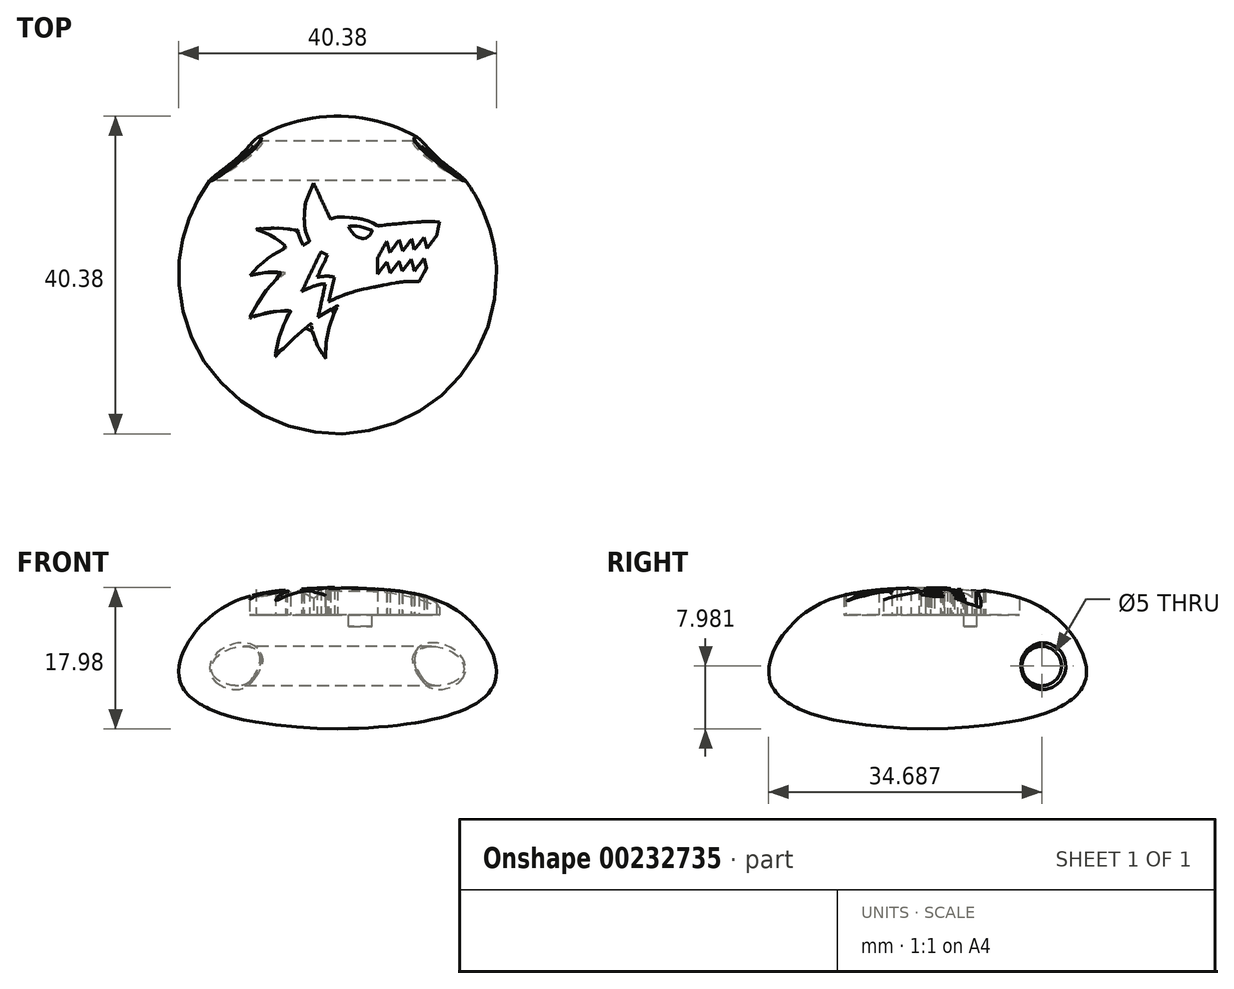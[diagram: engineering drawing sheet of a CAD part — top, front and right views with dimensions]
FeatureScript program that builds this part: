
annotation { "Feature Type Name" : "Feature", "Feature Type Description" : "" }
export const myFeature = defineFeature(function(context is Context, id is Id, definition is map)
    precondition{}
    {
        {
            var Q0;
            Q0=qCreatedBy(makeId("Front.planeOp"),FACE);
            var sketch = newSketch(context, id + "F0", { "sketchPlane" : qUnion([Q0])});
            skFitSpline(sketch, "E0", {"points": [v(0, 12) * mm, v(15.05, 9.11) * mm, v(20, 0) * mm, v(0, -6) * mm], "startDerivative": vector(53.57, -2.67) * mm, "endDerivative": vector(-80.04, -1.37) * mm});
            skLineSegment(sketch, "E1", {"start": v(0, 0) * mm, "end": v(0, -6) * mm});
            skLineSegment(sketch, "E2", {"start": v(0, 0) * mm, "end": v(0, 12) * mm});
            skLineSegment(sketch, "E3", {"start": v(0, 0) * mm, "end": v(20, 0) * mm});
            skSolve(sketch);
        }
        {
            var Q0;
            Q0 = qSketchRegion(id + "F0", true);
            var Q1;
            Q1=sQuery(id+"F0.wireOp",EDGE,"E2");
            revolve(context, id + "F1", {"entities" : qUnion([Q0]), "axis" : qUnion([Q1]), "revolveType" : RevolveType.FULL});
        }
        {
            var Q0;
            Q0=qCreatedBy(makeId("Top.planeOp"),FACE);
            var sketch = newSketch(context, id + "F2", { "sketchPlane" : qUnion([Q0])});
            skLineSegment(sketch, "E4", {"start": v(-3.05, 11.68) * mm, "end": v(-0.92, 7.1) * mm});
            skFitSpline(sketch, "E5", {"points": [v(-0.92, 7.1) * mm, v(0, 7.34) * mm, v(1.82, 7.27) * mm, v(3.9, 6.84) * mm, v(5.2, 6.21) * mm, v(5.35, 6.24) * mm, v(7.78, 6.52) * mm, v(10.2, 6.73) * mm, v(12.15, 6.78) * mm, v(12.94, 6.73) * mm], "startDerivative": vector(9.2, 3.23) * mm, "endDerivative": vector(8.4, -0.74) * mm});
            skLineSegment(sketch, "E6", {"start": v(12.94, 6.73) * mm, "end": v(12.59, 5) * mm});
            skLineSegment(sketch, "E7", {"start": v(12.59, 5) * mm, "end": v(11.37, 3.38) * mm});
            skLineSegment(sketch, "E8", {"start": v(11.37, 3.38) * mm, "end": v(10.98, 4.75) * mm});
            skLineSegment(sketch, "E9", {"start": v(10.98, 4.75) * mm, "end": v(9.74, 3.2) * mm});
            skLineSegment(sketch, "E10", {"start": v(9.74, 3.2) * mm, "end": v(9.42, 4.54) * mm});
            skLineSegment(sketch, "E11", {"start": v(9.42, 4.54) * mm, "end": v(8.26, 3.04) * mm});
            skLineSegment(sketch, "E12", {"start": v(8.26, 3.04) * mm, "end": v(7.83, 4.46) * mm});
            skLineSegment(sketch, "E13", {"start": v(7.83, 4.46) * mm, "end": v(6.64, 2.83) * mm});
            skLineSegment(sketch, "E14", {"start": v(6.64, 2.83) * mm, "end": v(6.23, 4.27) * mm});
            skLineSegment(sketch, "E15", {"start": v(6.23, 4.27) * mm, "end": v(5.1, 2.17) * mm});
            skLineSegment(sketch, "E16", {"start": v(5.1, 2.17) * mm, "end": v(5.1, 0.13) * mm});
            skLineSegment(sketch, "E17", {"start": v(5.1, 0.13) * mm, "end": v(6.27, 1.66) * mm});
            skLineSegment(sketch, "E18", {"start": v(6.27, 1.66) * mm, "end": v(6.68, 0.23) * mm});
            skLineSegment(sketch, "E19", {"start": v(6.68, 0.23) * mm, "end": v(7.8, 1.72) * mm});
            skLineSegment(sketch, "E20", {"start": v(7.8, 1.72) * mm, "end": v(8.21, 0.49) * mm});
            skLineSegment(sketch, "E21", {"start": v(8.21, 0.49) * mm, "end": v(9.35, 1.93) * mm});
            skLineSegment(sketch, "E22", {"start": v(9.35, 1.93) * mm, "end": v(9.77, 0.52) * mm});
            skLineSegment(sketch, "E23", {"start": v(9.77, 0.52) * mm, "end": v(10.96, 2.06) * mm});
            skLineSegment(sketch, "E24", {"start": v(10.96, 2.06) * mm, "end": v(11.28, 0.89) * mm});
            skLineSegment(sketch, "E25", {"start": v(11.28, 0.89) * mm, "end": v(10.35, -0.85) * mm});
            skFitSpline(sketch, "E26", {"points": [v(10.35, -0.85) * mm, v(8.53, -0.85) * mm, v(5.91, -1.28) * mm, v(3.45, -1.78) * mm, v(1.3, -2.36) * mm, v(-0.33, -3.02) * mm, v(-1.12, -3.4) * mm], "startDerivative": vector(-10.67, 0.52) * mm, "endDerivative": vector(-6.39, -3.07) * mm});
            skLineSegment(sketch, "E27", {"start": v(-1.12, -3.4) * mm, "end": v(-0.4, -0.29) * mm});
            skFitSpline(sketch, "E28", {"points": [v(-0.4, -0.29) * mm, v(-1.22, -0.16) * mm, v(-2.62, -0.29) * mm], "startDerivative": vector(-1.76, 0.4) * mm, "endDerivative": vector(-2.64, -0.38) * mm});
            skLineSegment(sketch, "E29", {"start": v(-2.62, -0.29) * mm, "end": v(-1.26, 2.51) * mm});
            skLineSegment(sketch, "E30", {"start": v(-1.26, 2.51) * mm, "end": v(-2.12, 2.93) * mm});
            skLineSegment(sketch, "E31", {"start": v(-2.12, 2.93) * mm, "end": v(-4.55, -2.1) * mm});
            skFitSpline(sketch, "E32", {"points": [v(-4.55, -2.1) * mm, v(-2.63, -1.3) * mm, v(-1.55, -1.12) * mm], "startDerivative": vector(3.52, 1.65) * mm, "endDerivative": vector(2.4, 0.22) * mm});
            skLineSegment(sketch, "E33", {"start": v(-1.55, -1.12) * mm, "end": v(-2.47, -5.36) * mm});
            skFitSpline(sketch, "E34", {"points": [v(-2.47, -5.36) * mm, v(-0.23, -4) * mm, v(0, -3.9) * mm, v(-0.33, -4.66) * mm, v(-0.9, -6.16) * mm, v(-1.38, -8.06) * mm, v(-1.55, -10.54) * mm, v(-1.54, -10.62) * mm, v(-2.36, -9.36) * mm, v(-3.15, -7.43) * mm, v(-3.34, -6.22) * mm, v(-3.37, -6.18) * mm, v(-4.47, -7.1) * mm, v(-5.62, -8.1) * mm, v(-6.75, -9.22) * mm, v(-7.78, -10.26) * mm, v(-7.88, -10.37) * mm, v(-7.35, -7.69) * mm, v(-6.04, -4.76) * mm, v(-5.98, -4.58) * mm, v(-8, -4.65) * mm, v(-9.52, -4.94) * mm, v(-11.06, -5.5) * mm, v(-11.2, -5.58) * mm, v(-10.47, -4.12) * mm, v(-9.42, -2.46) * mm, v(-8.21, -0.96) * mm, v(-6.73, 0.15) * mm, v(-6.62, 0.23) * mm, v(-8.57, 0.36) * mm, v(-10.77, 0) * mm, v(-11.13, -0.08) * mm], "startDerivative": vector(57.9, 34.46) * mm, "endDerivative": vector(-16.28, -3.46) * mm});
            skFitSpline(sketch, "E35", {"points": [v(-11.13, -0.08) * mm, v(-10.4, 0.74) * mm, v(-9.44, 1.65) * mm, v(-8.2, 2.57) * mm, v(-6.9, 3.27) * mm, v(-6.51, 3.44) * mm, v(-6.44, 3.45) * mm, v(-7.94, 4.7) * mm, v(-9.82, 5.6) * mm, v(-10.18, 5.73) * mm, v(-10.35, 5.8) * mm, v(-9.37, 5.88) * mm, v(-7.8, 5.95) * mm, v(-6.53, 5.87) * mm, v(-5.07, 5.68) * mm, v(-5.05, 5.68) * mm, v(-4.93, 5.07) * mm, v(-4.67, 4.37) * mm, v(-4.36, 3.79) * mm], "startDerivative": vector(11, 12.95) * mm, "endDerivative": vector(6.62, -11.9) * mm});
            skLineSegment(sketch, "E36", {"start": v(-4.36, 3.79) * mm, "end": v(-3.53, 4.26) * mm});
            skFitSpline(sketch, "E37", {"points": [v(-3.53, 4.26) * mm, v(-3.98, 5.26) * mm, v(-4.23, 7.12) * mm, v(-4.07, 9.06) * mm, v(-3.7, 10.17) * mm, v(-3.05, 11.68) * mm], "startDerivative": vector(-2.9, 5.39) * mm, "endDerivative": vector(3.33, 7.68) * mm});
            skFitSpline(sketch, "E38", {"points": [v(1.4, 6.17) * mm, v(2.11, 6.23) * mm, v(3.27, 6.04) * mm, v(4.22, 5.73) * mm, v(4.4, 5.65) * mm, v(4.2, 5.23) * mm, v(3.8, 4.81) * mm, v(3.2, 4.6) * mm, v(3.07, 4.65) * mm, v(2.76, 4.72) * mm, v(2, 5.25) * mm, v(1.46, 5.95) * mm, v(1.4, 6.17) * mm]});
            skSolve(sketch);
        }
        {
            var Q0;
            Q0 = qSketchRegion(id + "F2", true);
            extrude(context, id + "F3", {"entities" : qUnion([Q0]), "operationType" : NewBodyOperationType.REMOVE, "depth" : 25 * mm, "hasSecondDirection" : true, "secondDirectionOppositeDirection" : false, "secondDirectionDepth" : 8.5 * mm});
        }
        {
            var Q0;
            Q0=makeQuery(id+"F2.imprint","IMPRINT",FACE,{"disambiguationData":[TD([[makeQuery(id+"F2.imprint","IMPRINT",EDGE,{"derivedFrom":sQuery(id+"F2.wireOp",EDGE,"E38")}),-1.0]])]});
            extrude(context, id + "F4", {"entities" : qUnion([Q0]), "operationType" : NewBodyOperationType.REMOVE, "depth" : 25 * mm, "hasSecondDirection" : true, "secondDirectionOppositeDirection" : false, "secondDirectionDepth" : 7 * mm});
        }
        {
            var Q0;
            Q0=qCreatedBy(makeId("Right.planeOp"),FACE);
            var sketch = newSketch(context, id + "F5", { "sketchPlane" : qUnion([Q0])});
            skCircle(sketch, "E39", {"center": v(14.5, 1.98) * mm, "radius": 2.5 * mm});
            skSolve(sketch);
        }
        {
            var Q0;
            Q0 = qSketchRegion(id + "F5", true);
            var Q1;
            Q1=sQuery(id+"F5.wireOp",EDGE,"E39");
            extrude(context, id + "F6", {"entities" : qUnion([Q0]), "operationType" : NewBodyOperationType.REMOVE, "surfaceEntities" : qUnion([Q1]), "endBound" : BoundingType.THROUGH_ALL, "depth" : 25 * mm, "hasSecondDirection" : true, "secondDirectionBound" : SecondDirectionBoundingType.THROUGH_ALL, "secondDirectionOppositeDirection" : true, "secondDirectionDepth" : 25 * mm});
        }
        {
            var Q0;
            {var subQ32=sQuery(id+"F2.wireOp",EDGE,"E4");Q0=makeQuery(id+"F6.boolean.opBoolean","INTERSECT",EDGE,{"disambiguationData":[OD(0.0)],"derivedFrom":[makeQuery(id+"F3.boolean.opBoolean","SPLIT",FACE,{"disambiguationData":[TD([makeQuery(id+"F3.opExtrude","SWEPT_FACE",FACE,{"disambiguationData":[OSD([subQ32])]})])],"derivedFrom":makeQuery(id+"F1.opRevolve","SWEPT_FACE",FACE,{"disambiguationData":[OSD([sQuery(id+"F0.wireOp",EDGE,"E0")])]})}),makeQuery(id+"F6.opExtrude","SWEPT_FACE",FACE,{"disambiguationData":[OSD([sQuery(id+"F5.wireOp",EDGE,"E39")])]})]});}
            fillet(context, id + "F7", {"entities" : qUnion([Q0]), "radius" : .3 * mm, "tangentPropagation" : true, "allowEdgeOverflow" : false});
        }
        {
            var Q0;
            {var subQ32=sQuery(id+"F2.wireOp",EDGE,"E4");Q0=makeQuery(id+"F6.boolean.opBoolean","INTERSECT",EDGE,{"disambiguationData":[OD(1.0)],"derivedFrom":[makeQuery(id+"F3.boolean.opBoolean","SPLIT",FACE,{"disambiguationData":[TD([makeQuery(id+"F3.opExtrude","SWEPT_FACE",FACE,{"disambiguationData":[OSD([subQ32])]})])],"derivedFrom":makeQuery(id+"F1.opRevolve","SWEPT_FACE",FACE,{"disambiguationData":[OSD([sQuery(id+"F0.wireOp",EDGE,"E0")])]})}),makeQuery(id+"F6.opExtrude","SWEPT_FACE",FACE,{"disambiguationData":[OSD([sQuery(id+"F5.wireOp",EDGE,"E39")])]})]});}
            fillet(context, id + "F8", {"entities" : qUnion([Q0]), "radius" : .3 * mm, "tangentPropagation" : true, "allowEdgeOverflow" : false});
        }
    });
